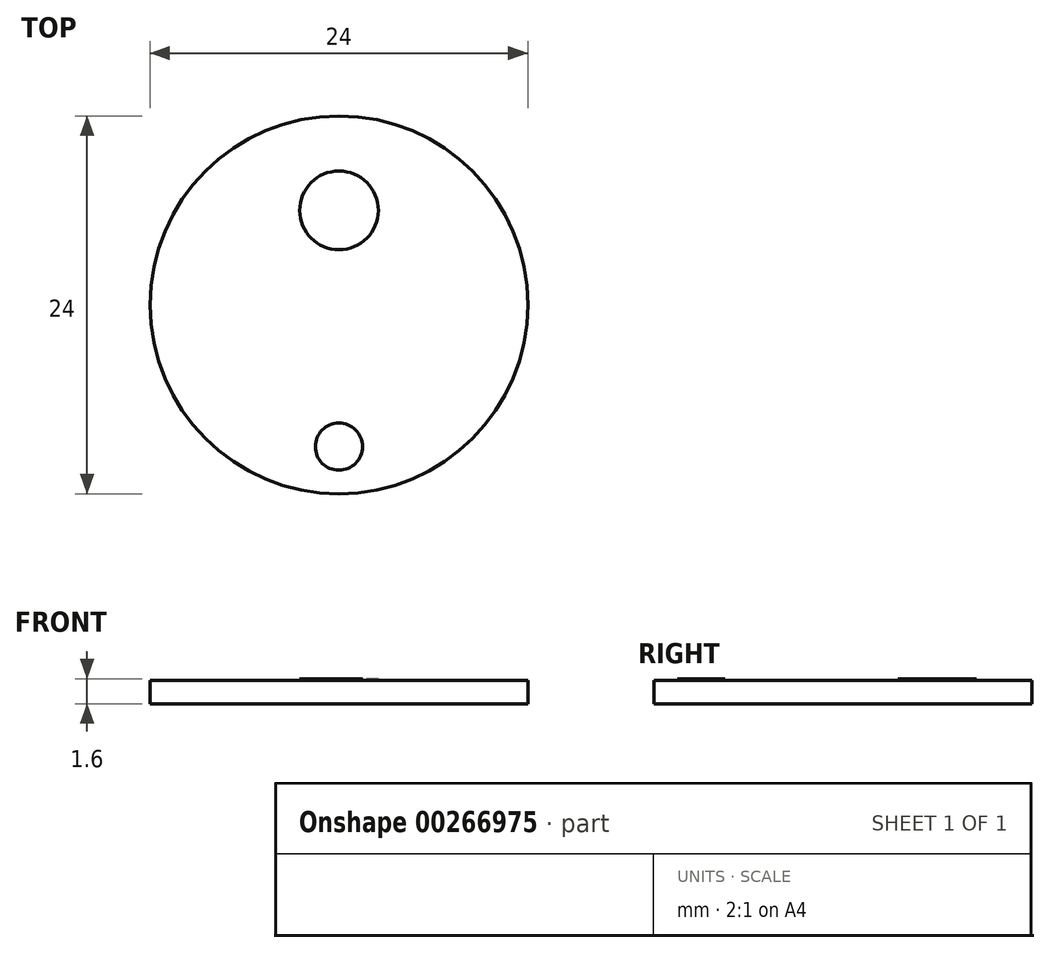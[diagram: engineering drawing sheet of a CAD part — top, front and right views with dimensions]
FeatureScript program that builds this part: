
annotation { "Feature Type Name" : "Feature", "Feature Type Description" : "" }
export const myFeature = defineFeature(function(context is Context, id is Id, definition is map)
    precondition{}
    {
        {
            var Q0;
            Q0=qCreatedBy(makeId("Top.planeOp"),FACE);
            var sketch = newSketch(context, id + "F0", { "sketchPlane" : qUnion([Q0])});
            skCircle(sketch, "E0", {"center": v(0, 0) * mm, "radius": 12 * mm});
            skSolve(sketch);
        }
        {
            var Q0;
            Q0=qSketchRegion(id+"F0",true);
            extrude(context, id + "F1", {"entities" : qUnion([Q0]), "depth" : 1.5 * mm});
        }
        {
            var Q0;
            Q0=makeQuery(id+"F1.opExtrude","CAP_FACE",FACE,{"disambiguationData":[OSD([sQuery(id+"F0.wireOp",EDGE,"E0")])],"isStart":false});
            var sketch = newSketch(context, id + "F2", { "sketchPlane" : qUnion([Q0])});
            skLineSegment(sketch, "E1", {"start": v(0, 0) * mm, "end": v(0, 6) * mm, "construction": true});
            skCircle(sketch, "E2", {"center": v(0, 6) * mm, "radius": 2.5 * mm});
            skLineSegment(sketch, "E3", {"start": v(0, 0) * mm, "end": v(0, -9) * mm, "construction": true});
            skCircle(sketch, "E4", {"center": v(0, -9) * mm, "radius": 1.5 * mm});
            skSolve(sketch);
        }
        {
            var Q0;
            Q0=makeQuery(id+"F2.imprint","IMPRINT",FACE,{"disambiguationData":[TD([[makeQuery(id+"F2.imprint","IMPRINT",EDGE,{"derivedFrom":sQuery(id+"F2.wireOp",EDGE,"E2")}),1.0]])]});
            var Q1;
            Q1=makeQuery(id+"F2.imprint","IMPRINT",FACE,{"disambiguationData":[TD([[makeQuery(id+"F2.imprint","IMPRINT",EDGE,{"derivedFrom":sQuery(id+"F2.wireOp",EDGE,"E4")}),1.0]])]});
            extrude(context, id + "F3", {"entities" : qUnion([Q0, Q1]), "operationType" : NewBodyOperationType.ADD, "depth" : 0.1 * mm});
        }
    });
